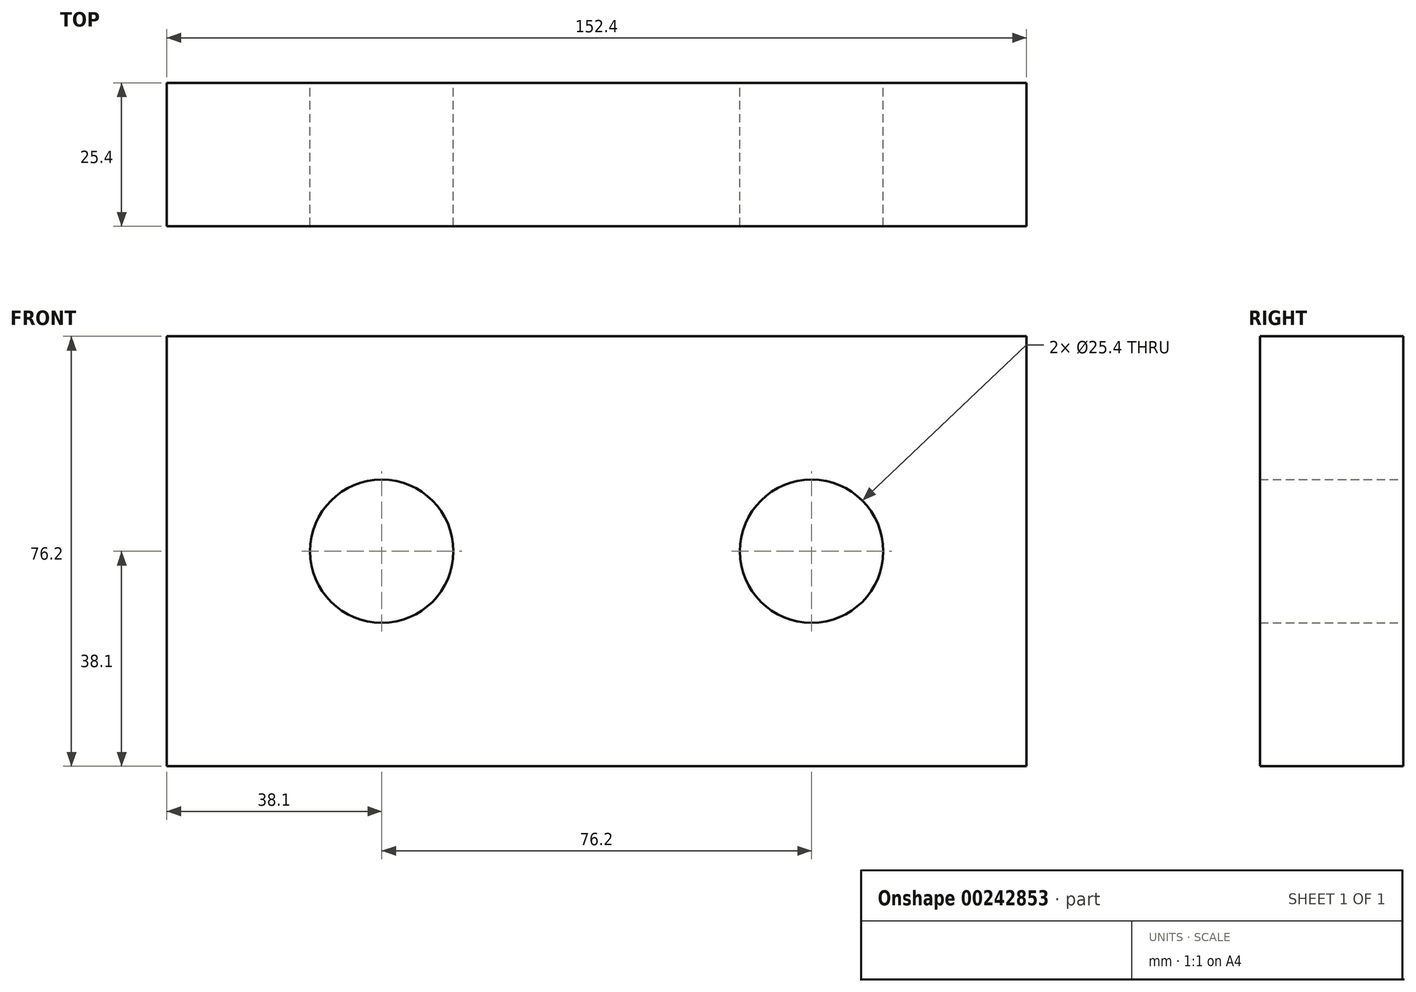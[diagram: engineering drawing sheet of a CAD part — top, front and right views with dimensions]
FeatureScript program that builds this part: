
annotation { "Feature Type Name" : "Feature", "Feature Type Description" : "" }
export const myFeature = defineFeature(function(context is Context, id is Id, definition is map)
    precondition{}
    {
        {
            var Q0;
            Q0=qCreatedBy(makeId("Front.planeOp"),FACE);
            var sketch = newSketch(context, id + "F0", { "sketchPlane" : qUnion([Q0])});
            skLineSegment(sketch, "E0.bottom", {"start": v(-76.2, -38.1) * mm, "end": v(76.2, -38.1) * mm});
            skLineSegment(sketch, "E0.top", {"start": v(-76.2, 38.1) * mm, "end": v(76.2, 38.1) * mm});
            skLineSegment(sketch, "E0.left", {"start": v(-76.2, -38.1) * mm, "end": v(-76.2, 38.1) * mm});
            skLineSegment(sketch, "E0.right", {"start": v(76.2, -38.1) * mm, "end": v(76.2, 38.1) * mm});
            skPoint(sketch, "E0.middle", {"position": v(0, 0) * mm});
            skCircle(sketch, "E1", {"center": v(-38.1, 0) * mm, "radius": 12.7 * mm});
            skCircle(sketch, "E2", {"center": v(38.1, 0) * mm, "radius": 12.7 * mm});
            skSolve(sketch);
        }
        {
            var Q0;
            Q0 = qSketchRegion(id + "F0", true);
            extrude(context, id + "F1", {"entities" : qUnion([Q0]), "depth" : 25.4 * mm});
        }
    });
